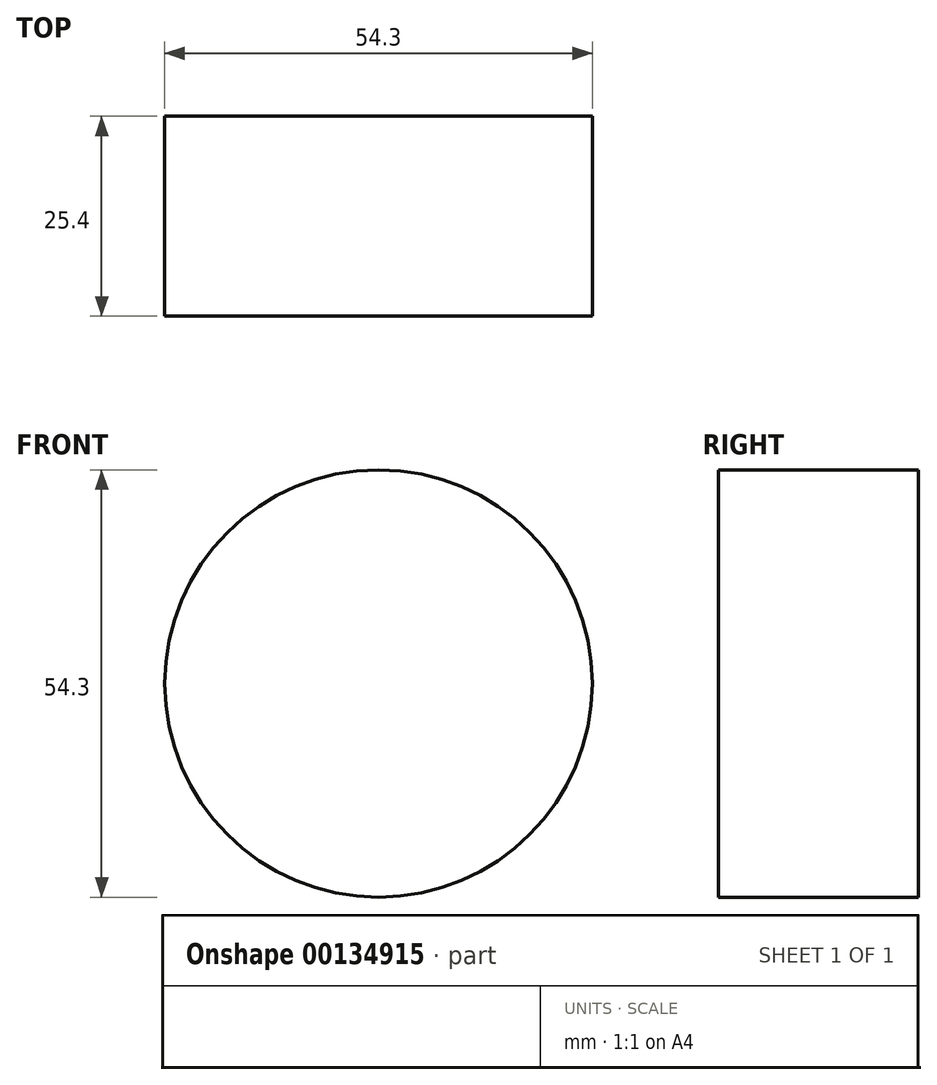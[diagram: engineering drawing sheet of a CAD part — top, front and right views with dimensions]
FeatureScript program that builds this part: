
annotation { "Feature Type Name" : "Feature", "Feature Type Description" : "" }
export const myFeature = defineFeature(function(context is Context, id is Id, definition is map)
    precondition{}
    {
        {
            var Q0;
            Q0=qCreatedBy(makeId("Front.planeOp"),FACE);
            var sketch = newSketch(context, id + "F0", { "sketchPlane" : qUnion([Q0])});
            skCircle(sketch, "E0", {"center": v(0, -1.75) * mm, "radius": 27.15 * mm});
            skSolve(sketch);
        }
        {
            var Q0;
            Q0 = qSketchRegion(id + "F0", true);
            extrude(context, id + "F1", {"entities" : qUnion([Q0]), "depth" : 25.4 * mm});
        }
    });
